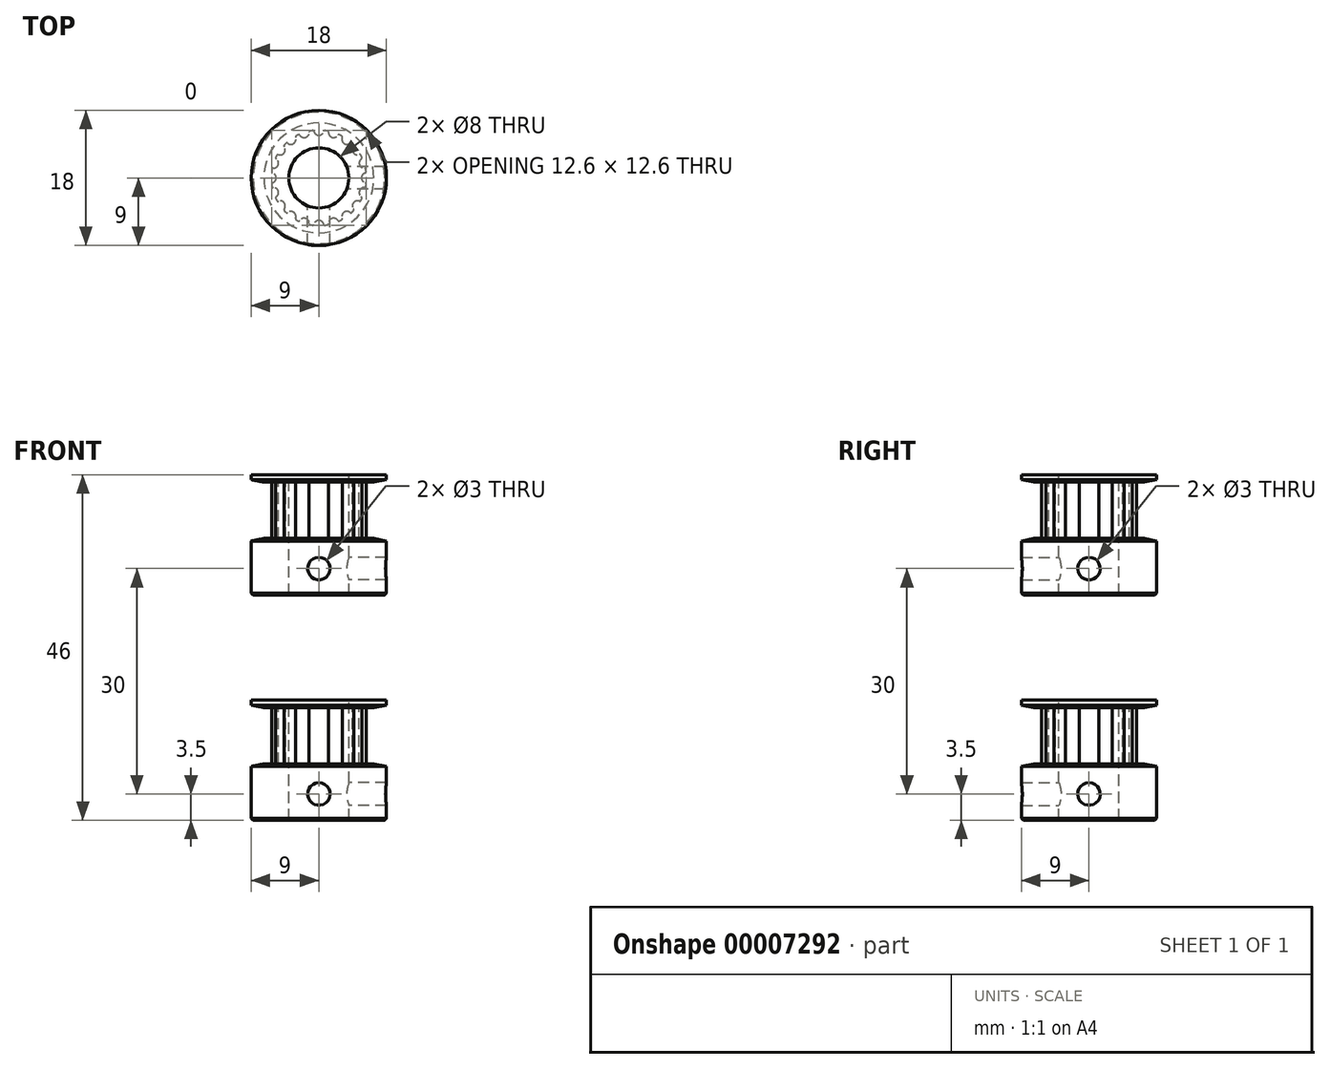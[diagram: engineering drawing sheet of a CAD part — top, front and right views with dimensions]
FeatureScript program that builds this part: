
annotation { "Feature Type Name" : "Feature", "Feature Type Description" : "" }
export const myFeature = defineFeature(function(context is Context, id is Id, definition is map)
    precondition{}
    {
        {
            var Q0;
            Q0=qCreatedBy(makeId("Front.planeOp"),FACE);
            var sketch = newSketch(context, id + "F0", { "sketchPlane" : qUnion([Q0])});
            skLineSegment(sketch, "E0", {"start": v(0, 0) * mm, "end": v(0, 16) * mm});
            skLineSegment(sketch, "E1", {"start": v(0, 16) * mm, "end": v(9, 16) * mm});
            skLineSegment(sketch, "E2", {"start": v(9, 16) * mm, "end": v(9, 15.33) * mm});
            skLineSegment(sketch, "E3", {"start": v(9, 15.33) * mm, "end": v(7.31, 15) * mm});
            skLineSegment(sketch, "E4", {"start": v(7.31, 15) * mm, "end": v(6.35, 15) * mm});
            skLineSegment(sketch, "E5", {"start": v(6.35, 15) * mm, "end": v(6.35, 7.5) * mm});
            skLineSegment(sketch, "E6", {"start": v(6.35, 7.5) * mm, "end": v(7.31, 7.5) * mm});
            skLineSegment(sketch, "E7", {"start": v(7.31, 7.5) * mm, "end": v(9, 7.17) * mm});
            skLineSegment(sketch, "E8", {"start": v(9, 7.17) * mm, "end": v(9, 0) * mm});
            skLineSegment(sketch, "E9", {"start": v(9, 0) * mm, "end": v(0, 0) * mm});
            skLineSegment(sketch, "E10", {"start": v(9, 15.33) * mm, "end": v(9, 7.17) * mm, "construction": true});
            skLineSegment(sketch, "E11", {"start": v(0, 16) * mm, "end": v(0, 19.19) * mm, "construction": true});
            skLineSegment(sketch, "E12.MirrorCS", {"start": v(-9, 0) * mm, "end": v(0, 0) * mm, "construction": true});
            skLineSegment(sketch, "E13.MirrorCS", {"start": v(-9, 7.17) * mm, "end": v(-9, 0) * mm, "construction": true});
            skLineSegment(sketch, "E14.MirrorCS", {"start": v(-7.31, 7.5) * mm, "end": v(-9, 7.17) * mm, "construction": true});
            skLineSegment(sketch, "E15.MirrorCS", {"start": v(-6.35, 7.5) * mm, "end": v(-7.31, 7.5) * mm, "construction": true});
            skLineSegment(sketch, "E16.MirrorCS", {"start": v(-6.35, 15) * mm, "end": v(-6.35, 7.5) * mm, "construction": true});
            skLineSegment(sketch, "E17.MirrorCS", {"start": v(-7.31, 15) * mm, "end": v(-6.35, 15) * mm, "construction": true});
            skLineSegment(sketch, "E18.MirrorCS", {"start": v(-9, 16) * mm, "end": v(-9, 15.33) * mm, "construction": true});
            skLineSegment(sketch, "E19.MirrorCS", {"start": v(0, 16) * mm, "end": v(-9, 16) * mm, "construction": true});
            skLineSegment(sketch, "E20.MirrorCS", {"start": v(-9, 15.33) * mm, "end": v(-7.31, 15) * mm, "construction": true});
            skLineSegment(sketch, "E21", {"start": v(7.31, 15) * mm, "end": v(7.31, 7.5) * mm, "construction": true});
            skSolve(sketch);
        }
        {
            var Q0;
            Q0 = qSketchRegion(id + "F0", true);
            var Q1;
            Q1=sQuery(id+"F0.wireOp",EDGE,"E11");
            revolve(context, id + "F1", {"entities" : qUnion([Q0]), "axis" : qUnion([Q1]), "revolveType" : RevolveType.FULL});
        }
        {
            var Q0;
            Q0=makeQuery(id+"F1.opRevolve","SWEPT_FACE",FACE,{"disambiguationData":[OSD([sQuery(id+"F0.wireOp",EDGE,"E4")])]});
            var sketch = newSketch(context, id + "F2", { "sketchPlane" : qUnion([Q0])});
            skCircle(sketch, "E22.0", {"center": v(0, 0) * mm, "radius": 6.35 * mm, "construction": true});
            skLineSegment(sketch, "E23", {"start": v(0, 0) * mm, "end": v(0, -6.35) * mm, "construction": true});
            skCircle(sketch, "E24", {"center": v(0, -6.35) * mm, "radius": 0.68 * mm});
            skCircle(sketch, "E25.1.0", {"center": v(1.96, -6.04) * mm, "radius": 0.68 * mm});
            skCircle(sketch, "E25.2.0", {"center": v(3.73, -5.14) * mm, "radius": 0.68 * mm});
            skCircle(sketch, "E25.3.0", {"center": v(5.14, -3.73) * mm, "radius": 0.68 * mm});
            skCircle(sketch, "E25.4.0", {"center": v(6.04, -1.96) * mm, "radius": 0.68 * mm});
            skCircle(sketch, "E25.5.0", {"center": v(6.35, 0) * mm, "radius": 0.68 * mm});
            skCircle(sketch, "E25.6.0", {"center": v(6.04, 1.96) * mm, "radius": 0.68 * mm});
            skCircle(sketch, "E25.7.0", {"center": v(5.14, 3.73) * mm, "radius": 0.67 * mm});
            skCircle(sketch, "E25.8.0", {"center": v(3.73, 5.14) * mm, "radius": 0.68 * mm});
            skCircle(sketch, "E25.9.0", {"center": v(1.96, 6.04) * mm, "radius": 0.68 * mm});
            skCircle(sketch, "E25.10.0", {"center": v(0, 6.35) * mm, "radius": 0.68 * mm});
            skCircle(sketch, "E25.11.0", {"center": v(-1.96, 6.04) * mm, "radius": 0.68 * mm});
            skCircle(sketch, "E25.12.0", {"center": v(-3.73, 5.14) * mm, "radius": 0.68 * mm});
            skCircle(sketch, "E25.13.0", {"center": v(-5.14, 3.73) * mm, "radius": 0.68 * mm});
            skCircle(sketch, "E25.14.0", {"center": v(-6.04, 1.96) * mm, "radius": 0.68 * mm});
            skCircle(sketch, "E25.15.0", {"center": v(-6.35, 0) * mm, "radius": 0.68 * mm});
            skCircle(sketch, "E25.16.0", {"center": v(-6.04, -1.96) * mm, "radius": 0.68 * mm});
            skCircle(sketch, "E25.17.0", {"center": v(-5.14, -3.73) * mm, "radius": 0.68 * mm});
            skCircle(sketch, "E25.18.0", {"center": v(-3.73, -5.14) * mm, "radius": 0.68 * mm});
            skCircle(sketch, "E25.19.0", {"center": v(-1.96, -6.04) * mm, "radius": 0.68 * mm});
            skSolve(sketch);
        }
        {
            var Q0;
            Q0 = qSketchRegion(id + "F2", true);
            var Q1;
            Q1=makeQuery(id+"F1.opRevolve","SWEPT_FACE",FACE,{"disambiguationData":[OSD([sQuery(id+"F0.wireOp",EDGE,"E6")])]});
            extrude(context, id + "F3", {"entities" : qUnion([Q0]), "operationType" : NewBodyOperationType.REMOVE, "endBound" : BoundingType.UP_TO_SURFACE, "endBoundEntityFace" : qUnion([Q1]), "depth" : 25 * mm});
        }
        {
            var Q0;
            Q0=qCreatedBy(makeId("Front.planeOp"),FACE);
            var sketch = newSketch(context, id + "F4", { "sketchPlane" : qUnion([Q0])});
            skLineSegment(sketch, "E26", {"start": v(0, 0) * mm, "end": v(0, 3.5) * mm, "construction": true});
            skCircle(sketch, "E27", {"center": v(0, 3.5) * mm, "radius": 1.5 * mm});
            skSolve(sketch);
        }
        {
            var Q0;
            Q0 = qSketchRegion(id + "F4", true);
            extrude(context, id + "F5", {"entities" : qUnion([Q0]), "operationType" : NewBodyOperationType.REMOVE, "endBound" : BoundingType.THROUGH_ALL, "depth" : 25 * mm});
        }
        {
            var Q0;
            Q0=qCreatedBy(makeId("Right.planeOp"),FACE);
            var sketch = newSketch(context, id + "F6", { "sketchPlane" : qUnion([Q0])});
            skLineSegment(sketch, "E28", {"start": v(0, 2) * mm, "end": v(-9, 2) * mm, "construction": true});
            skLineSegment(sketch, "E29", {"start": v(-9, 5) * mm, "end": v(0, 5) * mm, "construction": true});
            skLineSegment(sketch, "E30", {"start": v(0, 0) * mm, "end": v(0, 2) * mm, "construction": true});
            skLineSegment(sketch, "E31", {"start": v(0, 5) * mm, "end": v(0, 2) * mm, "construction": true});
            skCircle(sketch, "E32", {"center": v(0, 3.5) * mm, "radius": 1.5 * mm});
            skSolve(sketch);
        }
        {
            var Q0;
            Q0 = qSketchRegion(id + "F6", true);
            extrude(context, id + "F7", {"entities" : qUnion([Q0]), "operationType" : NewBodyOperationType.REMOVE, "endBound" : BoundingType.THROUGH_ALL, "depth" : 25 * mm});
        }
        {
            var Q0;
            Q0=makeQuery(id+"F3.boolean.opBoolean","INTERSECT",EDGE,{"disambiguationData":[OD(1.0)],"derivedFrom":[makeQuery(id+"F1.opRevolve","SWEPT_FACE",FACE,{"disambiguationData":[OSD([sQuery(id+"F0.wireOp",EDGE,"E5")])]}),makeQuery(id+"F3.opExtrude","SWEPT_FACE",FACE,{"disambiguationData":[OSD([sQuery(id+"F2.wireOp",EDGE,"E25.12.0")])]})]});
            var Q1;
            Q1=makeQuery(id+"F3.boolean.opBoolean","INTERSECT",EDGE,{"disambiguationData":[OD(0.0)],"derivedFrom":[makeQuery(id+"F1.opRevolve","SWEPT_FACE",FACE,{"disambiguationData":[OSD([sQuery(id+"F0.wireOp",EDGE,"E5")])]}),makeQuery(id+"F3.opExtrude","SWEPT_FACE",FACE,{"disambiguationData":[OSD([sQuery(id+"F2.wireOp",EDGE,"E25.12.0")])]})]});
            var Q2;
            Q2=makeQuery(id+"F3.boolean.opBoolean","INTERSECT",EDGE,{"disambiguationData":[OD(1.0)],"derivedFrom":[makeQuery(id+"F1.opRevolve","SWEPT_FACE",FACE,{"disambiguationData":[OSD([sQuery(id+"F0.wireOp",EDGE,"E5")])]}),makeQuery(id+"F3.opExtrude","SWEPT_FACE",FACE,{"disambiguationData":[OSD([sQuery(id+"F2.wireOp",EDGE,"E25.11.0")])]})]});
            var Q3;
            Q3=makeQuery(id+"F3.boolean.opBoolean","INTERSECT",EDGE,{"disambiguationData":[OD(0.0)],"derivedFrom":[makeQuery(id+"F1.opRevolve","SWEPT_FACE",FACE,{"disambiguationData":[OSD([sQuery(id+"F0.wireOp",EDGE,"E5")])]}),makeQuery(id+"F3.opExtrude","SWEPT_FACE",FACE,{"disambiguationData":[OSD([sQuery(id+"F2.wireOp",EDGE,"E25.11.0")])]})]});
            var Q4;
            Q4=makeQuery(id+"F3.boolean.opBoolean","INTERSECT",EDGE,{"disambiguationData":[OD(1.0)],"derivedFrom":[makeQuery(id+"F1.opRevolve","SWEPT_FACE",FACE,{"disambiguationData":[OSD([sQuery(id+"F0.wireOp",EDGE,"E5")])]}),makeQuery(id+"F3.opExtrude","SWEPT_FACE",FACE,{"disambiguationData":[OSD([sQuery(id+"F2.wireOp",EDGE,"E25.10.0")])]})]});
            var Q5;
            Q5=makeQuery(id+"F3.boolean.opBoolean","INTERSECT",EDGE,{"disambiguationData":[OD(0.0)],"derivedFrom":[makeQuery(id+"F1.opRevolve","SWEPT_FACE",FACE,{"disambiguationData":[OSD([sQuery(id+"F0.wireOp",EDGE,"E5")])]}),makeQuery(id+"F3.opExtrude","SWEPT_FACE",FACE,{"disambiguationData":[OSD([sQuery(id+"F2.wireOp",EDGE,"E25.10.0")])]})]});
            var Q6;
            Q6=makeQuery(id+"F3.boolean.opBoolean","INTERSECT",EDGE,{"disambiguationData":[OD(1.0)],"derivedFrom":[makeQuery(id+"F1.opRevolve","SWEPT_FACE",FACE,{"disambiguationData":[OSD([sQuery(id+"F0.wireOp",EDGE,"E5")])]}),makeQuery(id+"F3.opExtrude","SWEPT_FACE",FACE,{"disambiguationData":[OSD([sQuery(id+"F2.wireOp",EDGE,"E25.9.0")])]})]});
            var Q7;
            Q7=makeQuery(id+"F3.boolean.opBoolean","INTERSECT",EDGE,{"disambiguationData":[OD(0.0)],"derivedFrom":[makeQuery(id+"F1.opRevolve","SWEPT_FACE",FACE,{"disambiguationData":[OSD([sQuery(id+"F0.wireOp",EDGE,"E5")])]}),makeQuery(id+"F3.opExtrude","SWEPT_FACE",FACE,{"disambiguationData":[OSD([sQuery(id+"F2.wireOp",EDGE,"E25.9.0")])]})]});
            var Q8;
            Q8=makeQuery(id+"F3.boolean.opBoolean","INTERSECT",EDGE,{"disambiguationData":[OD(1.0)],"derivedFrom":[makeQuery(id+"F1.opRevolve","SWEPT_FACE",FACE,{"disambiguationData":[OSD([sQuery(id+"F0.wireOp",EDGE,"E5")])]}),makeQuery(id+"F3.opExtrude","SWEPT_FACE",FACE,{"disambiguationData":[OSD([sQuery(id+"F2.wireOp",EDGE,"E25.8.0")])]})]});
            var Q9;
            Q9=makeQuery(id+"F3.boolean.opBoolean","INTERSECT",EDGE,{"disambiguationData":[OD(0.0)],"derivedFrom":[makeQuery(id+"F1.opRevolve","SWEPT_FACE",FACE,{"disambiguationData":[OSD([sQuery(id+"F0.wireOp",EDGE,"E5")])]}),makeQuery(id+"F3.opExtrude","SWEPT_FACE",FACE,{"disambiguationData":[OSD([sQuery(id+"F2.wireOp",EDGE,"E25.8.0")])]})]});
            var Q10;
            Q10=makeQuery(id+"F3.boolean.opBoolean","INTERSECT",EDGE,{"disambiguationData":[OD(1.0)],"derivedFrom":[makeQuery(id+"F1.opRevolve","SWEPT_FACE",FACE,{"disambiguationData":[OSD([sQuery(id+"F0.wireOp",EDGE,"E5")])]}),makeQuery(id+"F3.opExtrude","SWEPT_FACE",FACE,{"disambiguationData":[OSD([sQuery(id+"F2.wireOp",EDGE,"E25.7.0")])]})]});
            var Q11;
            Q11=makeQuery(id+"F3.boolean.opBoolean","INTERSECT",EDGE,{"disambiguationData":[OD(0.0)],"derivedFrom":[makeQuery(id+"F1.opRevolve","SWEPT_FACE",FACE,{"disambiguationData":[OSD([sQuery(id+"F0.wireOp",EDGE,"E5")])]}),makeQuery(id+"F3.opExtrude","SWEPT_FACE",FACE,{"disambiguationData":[OSD([sQuery(id+"F2.wireOp",EDGE,"E25.7.0")])]})]});
            var Q12;
            Q12=makeQuery(id+"F3.boolean.opBoolean","INTERSECT",EDGE,{"disambiguationData":[OD(1.0)],"derivedFrom":[makeQuery(id+"F1.opRevolve","SWEPT_FACE",FACE,{"disambiguationData":[OSD([sQuery(id+"F0.wireOp",EDGE,"E5")])]}),makeQuery(id+"F3.opExtrude","SWEPT_FACE",FACE,{"disambiguationData":[OSD([sQuery(id+"F2.wireOp",EDGE,"E25.6.0")])]})]});
            var Q13;
            Q13=makeQuery(id+"F3.boolean.opBoolean","INTERSECT",EDGE,{"disambiguationData":[OD(0.0)],"derivedFrom":[makeQuery(id+"F1.opRevolve","SWEPT_FACE",FACE,{"disambiguationData":[OSD([sQuery(id+"F0.wireOp",EDGE,"E5")])]}),makeQuery(id+"F3.opExtrude","SWEPT_FACE",FACE,{"disambiguationData":[OSD([sQuery(id+"F2.wireOp",EDGE,"E25.6.0")])]})]});
            var Q14;
            Q14=makeQuery(id+"F3.boolean.opBoolean","INTERSECT",EDGE,{"disambiguationData":[OD(1.0)],"derivedFrom":[makeQuery(id+"F1.opRevolve","SWEPT_FACE",FACE,{"disambiguationData":[OSD([sQuery(id+"F0.wireOp",EDGE,"E5")])]}),makeQuery(id+"F3.opExtrude","SWEPT_FACE",FACE,{"disambiguationData":[OSD([sQuery(id+"F2.wireOp",EDGE,"E25.5.0")])]})]});
            var Q15;
            Q15=makeQuery(id+"F3.boolean.opBoolean","INTERSECT",EDGE,{"disambiguationData":[OD(0.0)],"derivedFrom":[makeQuery(id+"F1.opRevolve","SWEPT_FACE",FACE,{"disambiguationData":[OSD([sQuery(id+"F0.wireOp",EDGE,"E5")])]}),makeQuery(id+"F3.opExtrude","SWEPT_FACE",FACE,{"disambiguationData":[OSD([sQuery(id+"F2.wireOp",EDGE,"E25.5.0")])]})]});
            var Q16;
            Q16=makeQuery(id+"F3.boolean.opBoolean","INTERSECT",EDGE,{"disambiguationData":[OD(1.0)],"derivedFrom":[makeQuery(id+"F1.opRevolve","SWEPT_FACE",FACE,{"disambiguationData":[OSD([sQuery(id+"F0.wireOp",EDGE,"E5")])]}),makeQuery(id+"F3.opExtrude","SWEPT_FACE",FACE,{"disambiguationData":[OSD([sQuery(id+"F2.wireOp",EDGE,"E25.4.0")])]})]});
            var Q17;
            Q17=makeQuery(id+"F3.boolean.opBoolean","INTERSECT",EDGE,{"disambiguationData":[OD(0.0)],"derivedFrom":[makeQuery(id+"F1.opRevolve","SWEPT_FACE",FACE,{"disambiguationData":[OSD([sQuery(id+"F0.wireOp",EDGE,"E5")])]}),makeQuery(id+"F3.opExtrude","SWEPT_FACE",FACE,{"disambiguationData":[OSD([sQuery(id+"F2.wireOp",EDGE,"E25.4.0")])]})]});
            var Q18;
            Q18=makeQuery(id+"F3.boolean.opBoolean","INTERSECT",EDGE,{"disambiguationData":[OD(1.0)],"derivedFrom":[makeQuery(id+"F1.opRevolve","SWEPT_FACE",FACE,{"disambiguationData":[OSD([sQuery(id+"F0.wireOp",EDGE,"E5")])]}),makeQuery(id+"F3.opExtrude","SWEPT_FACE",FACE,{"disambiguationData":[OSD([sQuery(id+"F2.wireOp",EDGE,"E25.3.0")])]})]});
            var Q19;
            Q19=makeQuery(id+"F3.boolean.opBoolean","INTERSECT",EDGE,{"disambiguationData":[OD(0.0)],"derivedFrom":[makeQuery(id+"F1.opRevolve","SWEPT_FACE",FACE,{"disambiguationData":[OSD([sQuery(id+"F0.wireOp",EDGE,"E5")])]}),makeQuery(id+"F3.opExtrude","SWEPT_FACE",FACE,{"disambiguationData":[OSD([sQuery(id+"F2.wireOp",EDGE,"E25.3.0")])]})]});
            var Q20;
            Q20=makeQuery(id+"F3.boolean.opBoolean","INTERSECT",EDGE,{"disambiguationData":[OD(1.0)],"derivedFrom":[makeQuery(id+"F1.opRevolve","SWEPT_FACE",FACE,{"disambiguationData":[OSD([sQuery(id+"F0.wireOp",EDGE,"E5")])]}),makeQuery(id+"F3.opExtrude","SWEPT_FACE",FACE,{"disambiguationData":[OSD([sQuery(id+"F2.wireOp",EDGE,"E25.2.0")])]})]});
            var Q21;
            Q21=makeQuery(id+"F3.boolean.opBoolean","INTERSECT",EDGE,{"disambiguationData":[OD(0.0)],"derivedFrom":[makeQuery(id+"F1.opRevolve","SWEPT_FACE",FACE,{"disambiguationData":[OSD([sQuery(id+"F0.wireOp",EDGE,"E5")])]}),makeQuery(id+"F3.opExtrude","SWEPT_FACE",FACE,{"disambiguationData":[OSD([sQuery(id+"F2.wireOp",EDGE,"E25.2.0")])]})]});
            var Q22;
            Q22=makeQuery(id+"F3.boolean.opBoolean","INTERSECT",EDGE,{"disambiguationData":[OD(1.0)],"derivedFrom":[makeQuery(id+"F1.opRevolve","SWEPT_FACE",FACE,{"disambiguationData":[OSD([sQuery(id+"F0.wireOp",EDGE,"E5")])]}),makeQuery(id+"F3.opExtrude","SWEPT_FACE",FACE,{"disambiguationData":[OSD([sQuery(id+"F2.wireOp",EDGE,"E25.1.0")])]})]});
            var Q23;
            Q23=makeQuery(id+"F3.boolean.opBoolean","INTERSECT",EDGE,{"disambiguationData":[OD(0.0)],"derivedFrom":[makeQuery(id+"F1.opRevolve","SWEPT_FACE",FACE,{"disambiguationData":[OSD([sQuery(id+"F0.wireOp",EDGE,"E5")])]}),makeQuery(id+"F3.opExtrude","SWEPT_FACE",FACE,{"disambiguationData":[OSD([sQuery(id+"F2.wireOp",EDGE,"E25.1.0")])]})]});
            var Q24;
            Q24=makeQuery(id+"F3.boolean.opBoolean","INTERSECT",EDGE,{"disambiguationData":[OD(0.0)],"derivedFrom":[makeQuery(id+"F1.opRevolve","SWEPT_FACE",FACE,{"disambiguationData":[OSD([sQuery(id+"F0.wireOp",EDGE,"E5")])]}),makeQuery(id+"F3.opExtrude","SWEPT_FACE",FACE,{"disambiguationData":[OSD([sQuery(id+"F2.wireOp",EDGE,"E24")])]})]});
            var Q25;
            Q25=makeQuery(id+"F3.boolean.opBoolean","INTERSECT",EDGE,{"disambiguationData":[OD(1.0)],"derivedFrom":[makeQuery(id+"F1.opRevolve","SWEPT_FACE",FACE,{"disambiguationData":[OSD([sQuery(id+"F0.wireOp",EDGE,"E5")])]}),makeQuery(id+"F3.opExtrude","SWEPT_FACE",FACE,{"disambiguationData":[OSD([sQuery(id+"F2.wireOp",EDGE,"E24")])]})]});
            var Q26;
            Q26=makeQuery(id+"F3.boolean.opBoolean","INTERSECT",EDGE,{"disambiguationData":[OD(0.0)],"derivedFrom":[makeQuery(id+"F1.opRevolve","SWEPT_FACE",FACE,{"disambiguationData":[OSD([sQuery(id+"F0.wireOp",EDGE,"E5")])]}),makeQuery(id+"F3.opExtrude","SWEPT_FACE",FACE,{"disambiguationData":[OSD([sQuery(id+"F2.wireOp",EDGE,"E25.19.0")])]})]});
            var Q27;
            Q27=makeQuery(id+"F3.boolean.opBoolean","INTERSECT",EDGE,{"disambiguationData":[OD(1.0)],"derivedFrom":[makeQuery(id+"F1.opRevolve","SWEPT_FACE",FACE,{"disambiguationData":[OSD([sQuery(id+"F0.wireOp",EDGE,"E5")])]}),makeQuery(id+"F3.opExtrude","SWEPT_FACE",FACE,{"disambiguationData":[OSD([sQuery(id+"F2.wireOp",EDGE,"E25.19.0")])]})]});
            var Q28;
            Q28=makeQuery(id+"F3.boolean.opBoolean","INTERSECT",EDGE,{"disambiguationData":[OD(1.0)],"derivedFrom":[makeQuery(id+"F1.opRevolve","SWEPT_FACE",FACE,{"disambiguationData":[OSD([sQuery(id+"F0.wireOp",EDGE,"E5")])]}),makeQuery(id+"F3.opExtrude","SWEPT_FACE",FACE,{"disambiguationData":[OSD([sQuery(id+"F2.wireOp",EDGE,"E25.18.0")])]})]});
            var Q29;
            Q29=makeQuery(id+"F3.boolean.opBoolean","INTERSECT",EDGE,{"disambiguationData":[OD(0.0)],"derivedFrom":[makeQuery(id+"F1.opRevolve","SWEPT_FACE",FACE,{"disambiguationData":[OSD([sQuery(id+"F0.wireOp",EDGE,"E5")])]}),makeQuery(id+"F3.opExtrude","SWEPT_FACE",FACE,{"disambiguationData":[OSD([sQuery(id+"F2.wireOp",EDGE,"E25.18.0")])]})]});
            var Q30;
            Q30=makeQuery(id+"F3.boolean.opBoolean","INTERSECT",EDGE,{"disambiguationData":[OD(1.0)],"derivedFrom":[makeQuery(id+"F1.opRevolve","SWEPT_FACE",FACE,{"disambiguationData":[OSD([sQuery(id+"F0.wireOp",EDGE,"E5")])]}),makeQuery(id+"F3.opExtrude","SWEPT_FACE",FACE,{"disambiguationData":[OSD([sQuery(id+"F2.wireOp",EDGE,"E25.17.0")])]})]});
            var Q31;
            Q31=makeQuery(id+"F3.boolean.opBoolean","INTERSECT",EDGE,{"disambiguationData":[OD(0.0)],"derivedFrom":[makeQuery(id+"F1.opRevolve","SWEPT_FACE",FACE,{"disambiguationData":[OSD([sQuery(id+"F0.wireOp",EDGE,"E5")])]}),makeQuery(id+"F3.opExtrude","SWEPT_FACE",FACE,{"disambiguationData":[OSD([sQuery(id+"F2.wireOp",EDGE,"E25.17.0")])]})]});
            var Q32;
            Q32=makeQuery(id+"F3.boolean.opBoolean","INTERSECT",EDGE,{"disambiguationData":[OD(1.0)],"derivedFrom":[makeQuery(id+"F1.opRevolve","SWEPT_FACE",FACE,{"disambiguationData":[OSD([sQuery(id+"F0.wireOp",EDGE,"E5")])]}),makeQuery(id+"F3.opExtrude","SWEPT_FACE",FACE,{"disambiguationData":[OSD([sQuery(id+"F2.wireOp",EDGE,"E25.16.0")])]})]});
            var Q33;
            Q33=makeQuery(id+"F3.boolean.opBoolean","INTERSECT",EDGE,{"disambiguationData":[OD(0.0)],"derivedFrom":[makeQuery(id+"F1.opRevolve","SWEPT_FACE",FACE,{"disambiguationData":[OSD([sQuery(id+"F0.wireOp",EDGE,"E5")])]}),makeQuery(id+"F3.opExtrude","SWEPT_FACE",FACE,{"disambiguationData":[OSD([sQuery(id+"F2.wireOp",EDGE,"E25.16.0")])]})]});
            var Q34;
            Q34=makeQuery(id+"F3.boolean.opBoolean","INTERSECT",EDGE,{"disambiguationData":[OD(1.0)],"derivedFrom":[makeQuery(id+"F1.opRevolve","SWEPT_FACE",FACE,{"disambiguationData":[OSD([sQuery(id+"F0.wireOp",EDGE,"E5")])]}),makeQuery(id+"F3.opExtrude","SWEPT_FACE",FACE,{"disambiguationData":[OSD([sQuery(id+"F2.wireOp",EDGE,"E25.15.0")])]})]});
            var Q35;
            Q35=makeQuery(id+"F3.boolean.opBoolean","INTERSECT",EDGE,{"disambiguationData":[OD(0.0)],"derivedFrom":[makeQuery(id+"F1.opRevolve","SWEPT_FACE",FACE,{"disambiguationData":[OSD([sQuery(id+"F0.wireOp",EDGE,"E5")])]}),makeQuery(id+"F3.opExtrude","SWEPT_FACE",FACE,{"disambiguationData":[OSD([sQuery(id+"F2.wireOp",EDGE,"E25.15.0")])]})]});
            var Q36;
            Q36=makeQuery(id+"F3.boolean.opBoolean","INTERSECT",EDGE,{"disambiguationData":[OD(1.0)],"derivedFrom":[makeQuery(id+"F1.opRevolve","SWEPT_FACE",FACE,{"disambiguationData":[OSD([sQuery(id+"F0.wireOp",EDGE,"E5")])]}),makeQuery(id+"F3.opExtrude","SWEPT_FACE",FACE,{"disambiguationData":[OSD([sQuery(id+"F2.wireOp",EDGE,"E25.14.0")])]})]});
            var Q37;
            Q37=makeQuery(id+"F3.boolean.opBoolean","INTERSECT",EDGE,{"disambiguationData":[OD(0.0)],"derivedFrom":[makeQuery(id+"F1.opRevolve","SWEPT_FACE",FACE,{"disambiguationData":[OSD([sQuery(id+"F0.wireOp",EDGE,"E5")])]}),makeQuery(id+"F3.opExtrude","SWEPT_FACE",FACE,{"disambiguationData":[OSD([sQuery(id+"F2.wireOp",EDGE,"E25.13.0")])]})]});
            var Q38;
            Q38=makeQuery(id+"F3.boolean.opBoolean","INTERSECT",EDGE,{"disambiguationData":[OD(1.0)],"derivedFrom":[makeQuery(id+"F1.opRevolve","SWEPT_FACE",FACE,{"disambiguationData":[OSD([sQuery(id+"F0.wireOp",EDGE,"E5")])]}),makeQuery(id+"F3.opExtrude","SWEPT_FACE",FACE,{"disambiguationData":[OSD([sQuery(id+"F2.wireOp",EDGE,"E25.13.0")])]})]});
            var Q39;
            Q39=makeQuery(id+"F3.boolean.opBoolean","INTERSECT",EDGE,{"disambiguationData":[OD(0.0)],"derivedFrom":[makeQuery(id+"F1.opRevolve","SWEPT_FACE",FACE,{"disambiguationData":[OSD([sQuery(id+"F0.wireOp",EDGE,"E5")])]}),makeQuery(id+"F3.opExtrude","SWEPT_FACE",FACE,{"disambiguationData":[OSD([sQuery(id+"F2.wireOp",EDGE,"E25.14.0")])]})]});
            fillet(context, id + "F8", {"entities" : qUnion([Q0, Q1, Q2, Q3, Q4, Q5, Q6, Q7, Q8, Q9, Q10, Q11, Q12, Q13, Q14, Q15, Q16, Q17, Q18, Q19, Q20, Q21, Q22, Q23, Q24, Q25, Q26, Q27, Q28, Q29, Q30, Q31, Q32, Q33, Q34, Q35, Q36, Q37, Q38, Q39]), "radius" : .15 * mm, "tangentPropagation" : true, "allowEdgeOverflow" : false});
        }
        {
            var Q0;
            Q0=makeQuery(id+"F1.opRevolve","SWEPT_EDGE",EDGE,{"disambiguationData":[OSD([sQuery(id+"F0.wireOp",EDGE,"E8"),sQuery(id+"F0.wireOp",EDGE,"E9")])]});
            chamfer(context, id + "F9", {"entities" : qUnion([Q0]), "width" : .25 * mm, "tangentPropagation" : true});
        }
        {
            var Q0;
            Q0=makeQuery(id+"F1.opRevolve","SWEPT_BODY",BODY,{"disambiguationData":[OSD([sQuery(id+"F0.wireOp",EDGE,"E0"),sQuery(id+"F0.wireOp",EDGE,"E1"),sQuery(id+"F0.wireOp",EDGE,"E2"),sQuery(id+"F0.wireOp",EDGE,"E3"),sQuery(id+"F0.wireOp",EDGE,"E4"),sQuery(id+"F0.wireOp",EDGE,"E5"),sQuery(id+"F0.wireOp",EDGE,"E6"),sQuery(id+"F0.wireOp",EDGE,"E7"),sQuery(id+"F0.wireOp",EDGE,"E8"),sQuery(id+"F0.wireOp",EDGE,"E9")])]});
            transform(context, id + "F10", {"entities" : qUnion([Q0]), "transformType" : TransformType.TRANSLATION_3D, "dx" : 0 * mm, "dy" : 0 * mm, "dz" : 30 * mm, "makeCopy" : true});
        }
        {
            var Q0;
            Q0=makeQuery(id+"F10.opPattern","COPY",FACE,{"derivedFrom":makeQuery(id+"F1.opRevolve","SWEPT_FACE",FACE,{"disambiguationData":[OSD([sQuery(id+"F0.wireOp",EDGE,"E1")])]}),"instanceName":"1"});
            var sketch = newSketch(context, id + "F11", { "sketchPlane" : qUnion([Q0])});
            skCircle(sketch, "E33", {"center": v(0, 0) * mm, "radius": 4 * mm});
            skSolve(sketch);
        }
        {
            var Q0;
            Q0 = qSketchRegion(id + "F11", true);
            extrude(context, id + "F12", {"entities" : qUnion([Q0]), "operationType" : NewBodyOperationType.REMOVE, "endBound" : BoundingType.THROUGH_ALL, "oppositeDirection" : true, "depth" : 25 * mm});
        }
        {
            var Q0;
            Q0=makeQuery(id+"F1.opRevolve","SWEPT_FACE",FACE,{"disambiguationData":[OSD([sQuery(id+"F0.wireOp",EDGE,"E1")])]});
            var sketch = newSketch(context, id + "F13", { "sketchPlane" : qUnion([Q0])});
            skCircle(sketch, "E34", {"center": v(0, 0) * mm, "radius": 2.5 * mm});
            skSolve(sketch);
        }
        {
            var Q0;
            Q0 = qSketchRegion(id + "F13", true);
            extrude(context, id + "F14", {"entities" : qUnion([Q0]), "operationType" : NewBodyOperationType.REMOVE, "endBound" : BoundingType.THROUGH_ALL, "oppositeDirection" : true, "depth" : 25 * mm});
        }
    });
